# Revit family: TYCO-FPP-Fireclass FC32 AC Repeater
name_source: partatom
category: Electrical Fixtures
revit_build: Autodesk Revit 2014 (Build: 20130308_1515(x64)
units: mm (PartAtom-declared; Revit-internal decimal feet)

## types (1)
- TYCO-FPP-Fireclass FC32 AC Repeater
    BODY = RAL
    Charger Size = 2.5A
    Conventional Sounder circuits = 2 x 2Amp
    D = 126 mm
    DISPLAY = DIS
    Description = Addressable AC Repeater Panel
    EMC/RFI = EN50130-4 & EN61000-6-3
    H = 370 mm
    Humidity = 90% relative Humidity
    Input Current = 0.9A
    Keynote = Up to 7 repeaters can be connected to the repeater terminals via the remote bus
    Manufacturer = Tyco
    Max Battery Size = 2 x 12V 7Ah
    Model = Fireclass - 557.200.706
    Operating Temp = -5ºC + 40ºC
    SWPAD = SWPAD
    Storage Temp = -20ºC + 70ºC
    Supply Voltage = 230VAC 50/60 Hz 24VDC
    Type Comments = The FireClass range of repeaters are designed for
use with the FireClass 32, 64 and 240 panel ranges.
    URL = https://fireclass.co.uk
    W = 325 mm

## geometry (parser evidence)
native form markers: Sweep x1
no freeform markers — native parametric forms only
